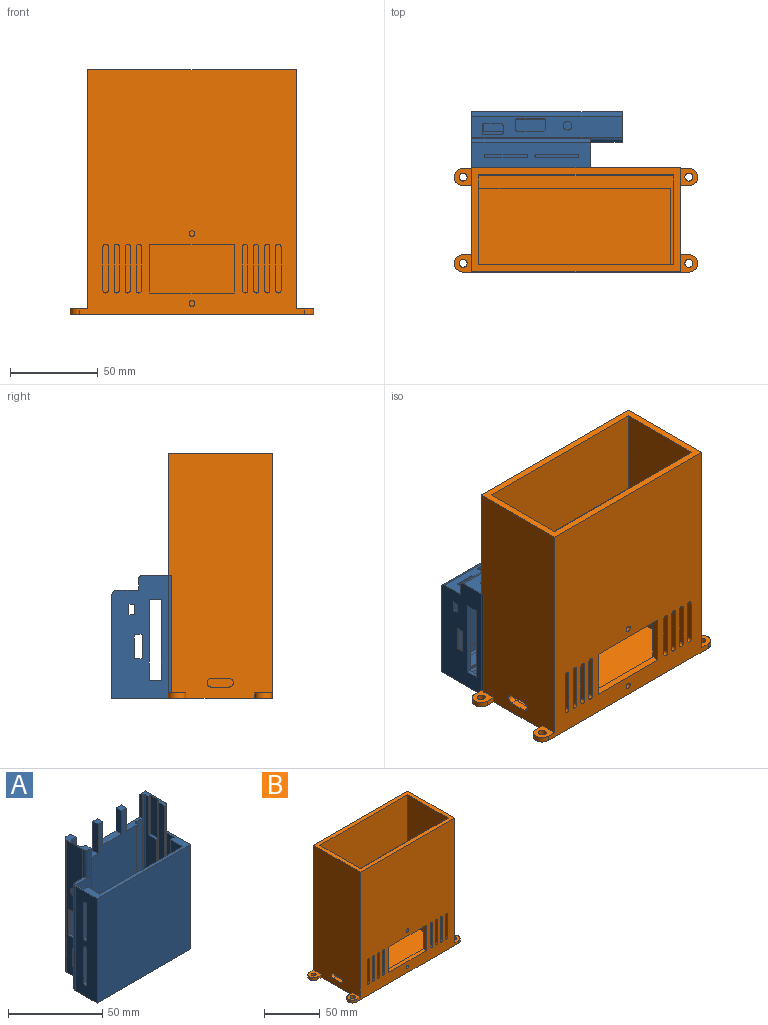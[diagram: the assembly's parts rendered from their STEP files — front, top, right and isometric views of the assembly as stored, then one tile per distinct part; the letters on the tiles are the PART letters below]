
ASSEMBLY  parts=2 mates=1
PART A: 148 faces, bbox 70.8x34.6x86.2 mm
  f0: plane 66x11mm, normal (1,0,0), area 577.7mm2, adj f3,f6,f10,f120,f130,f131,f132,f133
  f1: plane 41x1.75mm, normal (1,0,0), area 71.8mm2, adj f6,f7,f10,f143
  f2: plane 41x1.75mm, normal (-1,0,0), area 71.7mm2, adj f4,f5,f10,f147
  f3: plane 70.4x19.59mm, normal (0,0,1), area 249.6mm2, adj f0,f11,f30,f115,f116,f117,f120,f121
  f4: plane 41x2mm, normal (0,1,0), area 82mm2, adj f2,f10,f117,f147
  f5: plane 41x2mm, normal (0,-1,0), area 82mm2, adj f2,f10,f118,f147
  f6: plane 41x2mm, normal (0,1,0), area 82mm2, adj f0,f1,f10,f143
  f7: plane 41x2mm, normal (0,-1,0), area 82mm2, adj f1,f10,f119,f143
  f8: plane 69.5x5mm, normal (0,-1,0), area 281.5mm2, adj f24,f52,f54,f61,f63,f129
  f9: plane 70.4x34.2mm, normal (0,0,-1), area 1867.4mm2, adj f30,f31,f32,f36,f37,f38,f64,f92
  f10: plane 66x15mm, normal (0,0,1), area 613.2mm2, adj f0,f1,f2,f4,f5,f6,f7,f11
  f11: plane 83.8x11.7mm, normal (0,-1,0), area 674.1mm2, adj f3,f10,f13,f94,f119,f139,f141,f143
  f12: plane 85x4.48mm, normal (-1,0,0), area 369.3mm2, adj f24,f27,f35,f45,f79,f112,f114,f140
  f13: plane 17.2x5.6mm, normal (0,0,1), area 46.4mm2, adj f11,f15,f16,f21,f26,f31,f32,f44
  f14: plane 79.71x8.38mm, normal (-1,0,0), area 504.3mm2, adj f24,f34,f46,f61,f78,f104,f105
  f15: plane 85.1x50.2mm, normal (0,-1,0), area 3518.2mm2, adj f13,f20,f21,f25,f26,f27,f29,f50
  f16: plane 34.45x6.5mm, normal (1,0,0), area 199.8mm2, adj f13,f18,f19,f48,f49,f81
  f17: cone r=1.4mm half-angle=45deg, axis (1,0,0), area 0.8mm2, adj f20,f26,f72,f76,f98
  f18: cone r=3.25mm half-angle=45deg, axis (1,0,0), area 9.7mm2, adj f16,f26,f81,f82
  f19: cylinder r=2.5mm len=5mm, axis (1,0,0), area 12.6mm2, adj f16,f32
  f20: cylinder r=5mm len=6.38mm, axis (0,1,0), area 50.4mm2, adj f15,f17,f26,f27,f72,f80
  f21: cylinder r=1mm len=44.27mm, axis (0,0,-1), area 44.1mm2, adj f13,f15,f26,f82,f83,f86,f88
  f22: plane 5.42x4.59mm, normal (0,1,0), area 18.3mm2, adj f23,f27,f75,f77,f94,f97
  f23: plane 5.34x2.25mm, normal (1,0,0), area 9mm2, adj f22,f27,f47,f72,f75,f80
  f24: plane 17.2x4mm, normal (0,0,1), area 31.1mm2, adj f8,f12,f14,f30,f31,f33,f35,f54
  f25: plane 4.1x3.4mm, normal (0,0,1), area 13.9mm2, adj f15,f31,f56,f60
  f26: plane 80x8.63mm, normal (1,0,0), area 201.6mm2, adj f13,f15,f17,f18,f20,f21,f44,f81
  f27: plane 58.5x15.6mm, normal (0,0,1), area 568.3mm2, adj f12,f15,f20,f22,f23,f33,f34,f35
  f28: plane 7x5mm, normal (0,-1,0), area 22.5mm2, adj f46,f61,f63,f127
  f29: plane 4.1x3.9mm, normal (0,0,1), area 16mm2, adj f15,f31,f53,f57
  f30: plane 85.8x34.2mm, normal (1,0,0), area 2585.6mm2, adj f3,f9,f24,f31,f121,f140
  f31: plane 85.8x59.1mm, normal (0,1,0), area 4281.4mm2, adj f9,f13,f24,f25,f29,f30,f52,f53
  f32: plane 85.8x12mm, normal (-1,0,0), area 818mm2, adj f9,f13,f19,f39,f40,f41,f42,f64
  f33: plane 85x1.75mm, normal (-1,0,0), area 148.8mm2, adj f24,f27,f34,f35,f102
  f34: plane 60x6.09mm, normal (0,-1,0), area 62mm2, adj f14,f27,f33,f78,f105
  f35: plane 85x6.09mm, normal (0,1,0), area 82mm2, adj f12,f24,f27,f33,f79
  f36: plane 3.58x0.8mm, normal (-1,0,0), area 2.9mm2, adj f9,f27,f93,f114
  f37: plane 12x0.8mm, normal (0,-1,0), area 9.6mm2, adj f9,f27,f92,f93
  f38: plane 3.58x0.8mm, normal (1,0,0), area 2.9mm2, adj f9,f27,f92,f114
  f39: plane 5.4x1.2mm, normal (0,0,1), area 6.5mm2, adj f32,f67,f68,f85
  f40: plane 15.4x1.6mm, normal (0,-1,0), area 24.6mm2, adj f32,f50,f65,f68
  f41: plane 5.4x1.24mm, normal (0,0,-1), area 6.5mm2, adj f32,f65,f66,f88,f90
  f42: plane 15.4x1.2mm, normal (0,1,0), area 18.5mm2, adj f32,f66,f67,f89
  f43: cylinder r=5mm len=4.39mm, axis (0,-1,0), area 12.1mm2, adj f27,f77,f94,f110,f111
  f44: plane 68.42x2.89mm, normal (0,1,0), area 164mm2, adj f13,f26,f74,f94,f95,f101
  f45: plane 6.42x6.42mm, normal (-0.71,0,0.71), area 19.8mm2, adj f12,f27,f79,f112,f113
  f46: plane 9.3x6.42mm, normal (-0.71,0,0.71), area 75mm2, adj f14,f27,f28,f61,f78
  f47: plane 4.5x4.5mm, normal (0,-1,0), area 15.9mm2, adj f23,f27,f80
  f48: plane 31.2x0.48mm, normal (0,-1,0), area 15mm2, adj f13,f16,f49,f83
  f49: cylinder r=3.25mm len=2.33mm, axis (1,0,0), area 0.6mm2, adj f16,f48,f82
  f50: plane 16.26x0.13mm, normal (-1,0,0), area 2mm2, adj f15,f40,f65,f68
  f51: plane 70x0.5mm, normal (1,0,0), area 35mm2, adj f27,f52,f62,f63
  f52: plane 14.1x4.1mm, normal (0,0,1), area 44.3mm2, adj f8,f15,f31,f51,f53,f54,f62,f63
  f53: plane 15x4.1mm, normal (1,0,0), area 61.5mm2, adj f15,f29,f31,f52
  f54: plane 15x1.6mm, normal (-1,0,0), area 24mm2, adj f8,f24,f31,f52
  f55: plane 14.1x4.1mm, normal (0,0,1), area 57.8mm2, adj f15,f31,f56,f57
  f56: plane 15x4.1mm, normal (1,0,0), area 61.5mm2, adj f15,f25,f31,f55
  f57: plane 15x4.1mm, normal (-1,0,0), area 61.5mm2, adj f15,f29,f31,f55
  f58: plane 16.6x4.1mm, normal (0,0,1), area 68.1mm2, adj f15,f31,f59,f60
  f59: plane 19x4.1mm, normal (1,0,0), area 77.9mm2, adj f13,f15,f31,f58
  f60: plane 19x4.1mm, normal (-1,0,0), area 77.9mm2, adj f15,f25,f31,f58
  f61: cylinder r=1mm len=80mm, axis (0,0,-1), area 117mm2, adj f8,f14,f24,f28,f46,f126,f127,f129
  f62: cylinder r=1mm len=70mm, axis (0,0,1), area 110mm2, adj f15,f27,f51,f52
  f63: cylinder r=1mm len=70mm, axis (0,0,1), area 108.2mm2, adj f8,f27,f28,f51,f52,f127,f128,f129
  f64: cylinder r=2.6mm len=85.8mm, axis (0,0,-1), area 350.4mm2, adj f9,f13,f31,f32
  f65: cylinder r=0.8mm len=2.19mm, axis (1,0,0), area 2.1mm2, adj f15,f32,f40,f41,f50,f86
  f66: cylinder r=0.8mm len=1.2mm, axis (1,0,0), area 1.5mm2, adj f32,f41,f42,f91
  f67: cylinder r=0.8mm len=1.2mm, axis (1,0,0), area 1.5mm2, adj f32,f39,f42,f87
  f68: cylinder r=0.8mm len=1.6mm, axis (1,0,0), area 1.7mm2, adj f15,f32,f39,f40,f50,f84
  f69: plane 10x3.6mm, normal (0,1,0), area 36mm2, adj f32,f74,f75,f96
  f70: plane 4.2x1.2mm, normal (0,0,-1), area 5mm2, adj f32,f73,f74,f100
  f71: plane 10x1.2mm, normal (0,-1,0), area 12mm2, adj f32,f73,f76,f98
  f72: plane 4.5x1.9mm, normal (0,0,1), area 6.5mm2, adj f17,f20,f23,f32,f75,f76
  f73: cylinder r=1mm len=1.2mm, axis (1,0,0), area 1.9mm2, adj f32,f70,f71,f99
  f74: cylinder r=1mm len=3.6mm, axis (1,0,0), area 3.6mm2, adj f32,f44,f69,f70,f95,f101
  f75: cylinder r=1mm len=3.6mm, axis (1,0,0), area 4mm2, adj f22,f23,f32,f69,f72,f97
  f76: cylinder r=1mm len=1.2mm, axis (1,0,0), area 1.9mm2, adj f17,f32,f71,f72
  f77: cone r=4.5mm half-angle=45deg, axis (0,-1,0), area 3.5mm2, adj f22,f27,f43,f94
  f78: plane 6x6mm, normal (-0.5,-0.71,0.5), area 5.6mm2, adj f14,f27,f34,f46
  f79: plane 6x6mm, normal (-0.5,0.71,0.5), area 5.6mm2, adj f12,f27,f35,f45
  f80: cone r=4.5mm half-angle=45deg, axis (0,1,0), area 5.3mm2, adj f20,f23,f27,f47
  f81: plane 31.2x0.8mm, normal (0.71,0.71,0), area 35.3mm2, adj f13,f16,f18,f26
  f82: bspline ~2.9x1.24mm, area 2.4mm2, adj f18,f21,f49,f83
  f83: plane 31.2x0.59mm, normal (0.4,-0.92,0), area 20mm2, adj f13,f21,f48,f82
  f84: cone r=1.2mm half-angle=45deg, axis (1,0,0), area 0.4mm2, adj f15,f26,f68,f85
  f85: plane 5.4x0.4mm, normal (0.71,0,0.71), area 3.1mm2, adj f26,f39,f84,f87
  f86: bspline ~1.42x0.84mm, area 0.6mm2, adj f15,f21,f65,f88
  f87: cone r=1.2mm half-angle=45deg, axis (1,0,0), area 0.9mm2, adj f26,f67,f85,f89
  f88: cone r=1.4mm half-angle=45deg, axis (0,0,-1), area 0.2mm2, adj f21,f41,f86,f90
  f89: plane 15.4x0.4mm, normal (0.71,0.71,0), area 8.7mm2, adj f26,f42,f87,f91
  f90: plane 5.08x0.4mm, normal (0.71,0,-0.71), area 2.9mm2, adj f26,f41,f88,f91
  f91: cone r=1.2mm half-angle=45deg, axis (1,0,0), area 0.9mm2, adj f26,f66,f89,f90
  f92: cylinder r=1mm len=1mm, axis (0,0,-1), area 1.3mm2, adj f9,f27,f37,f38
  f93: cylinder r=1mm len=1mm, axis (0,0,-1), area 1.3mm2, adj f9,f27,f36,f37
  f94: plane 85.02x4.49mm, normal (1,0,0), area 364.7mm2, adj f11,f13,f22,f27,f43,f44,f77,f95
  f95: cone r=1.4mm half-angle=45deg, axis (1,0,0), area 0.6mm2, adj f44,f74,f94,f96
  f96: plane 10x0.4mm, normal (0.71,0.71,0), area 5.7mm2, adj f69,f94,f95,f97
  f97: cone r=1.4mm half-angle=45deg, axis (1,0,0), area 0.6mm2, adj f22,f75,f94,f96
  f98: plane 10x0.4mm, normal (0.71,-0.71,0), area 5.7mm2, adj f17,f26,f71,f99
  f99: cone r=1.4mm half-angle=45deg, axis (1,0,0), area 1.1mm2, adj f26,f73,f98,f100
  f100: plane 4.2x0.4mm, normal (0.71,0,-0.71), area 2.4mm2, adj f26,f70,f99,f101
  f101: cone r=1.4mm half-angle=45deg, axis (1,0,0), area 0.5mm2, adj f26,f44,f74,f100
  f102: plane 25x0.8mm, normal (0,1,0), area 20mm2, adj f24,f33,f103,f105
  f103: plane 25x6.3mm, normal (-1,0,0), area 157.5mm2, adj f24,f102,f104,f105
  f104: plane 25x1.6mm, normal (0,-1,0), area 40mm2, adj f14,f24,f103,f105
  f105: plane 6.3x1.6mm, normal (0,0,1), area 10.1mm2, adj f14,f34,f102,f103,f104
  f106: plane 3x0.8mm, normal (1,0,0), area 2.4mm2, adj f9,f27,f107,f108
  f107: plane 5.92x0.8mm, normal (0,1,0), area 4.7mm2, adj f9,f27,f106,f109
  f108: plane 5.92x0.8mm, normal (0,-1,0), area 4.7mm2, adj f9,f27,f106,f109
  f109: plane 3x0.8mm, normal (-1,0,0), area 2.4mm2, adj f9,f27,f107,f108
  f110: cylinder r=1mm len=4.39mm, axis (0,0,1), area 6.3mm2, adj f27,f43,f94,f111
  f111: plane 3.67x1.6mm, normal (0,-1,0), area 4.1mm2, adj f27,f43,f110
  f112: cylinder r=1mm len=6mm, axis (0,0,1), area 8.6mm2, adj f12,f27,f45,f113
  f113: plane 5x5mm, normal (0,-1,0), area 12.5mm2, adj f27,f45,f112
  f114: plane 55.3x43mm, normal (0,1,0), area 159.6mm2, adj f9,f10,f12,f27,f36,f38,f94,f118
  f115: plane 68x16.4mm, normal (-1,0,0), area 1016.9mm2, adj f3,f9,f121,f130,f131,f132,f133,f134
  f116: plane 68x6.17mm, normal (0,1,0), area 419.6mm2, adj f3,f9,f138,f139
  f117: plane 66x11mm, normal (-1,0,0), area 676mm2, adj f3,f4,f10,f120,f145,f147
  f118: plane 41x2.25mm, normal (-1,0,0), area 92.3mm2, adj f5,f10,f114,f147
  f119: plane 41x2.25mm, normal (1,0,0), area 92.3mm2, adj f7,f10,f11,f143
  f120: plane 66x62mm, normal (0,1,0), area 4092mm2, adj f0,f3,f10,f117
  f121: plane 70.4x68mm, normal (0,-1,0), area 4787.2mm2, adj f3,f9,f30,f115
  f122: plane 7x2mm, normal (-1,0,0), area 14mm2, adj f9,f10,f123,f124
  f123: plane 46.25x2mm, normal (0,-1,0), area 92.5mm2, adj f9,f10,f122,f125
  f124: plane 46.25x2mm, normal (0,1,0), area 92.5mm2, adj f9,f10,f122,f125
  f125: plane 7x2mm, normal (1,0,0), area 14mm2, adj f9,f10,f123,f124
  f126: plane 8.5x2mm, normal (-1,0,0), area 17mm2, adj f31,f61,f127,f129
  f127: plane 6x2mm, normal (0,0,1), area 9.7mm2, adj f28,f31,f61,f63,f126,f128
  f128: plane 8.5x1.62mm, normal (1,0,0), area 13.8mm2, adj f31,f63,f127,f129
  f129: plane 6x2mm, normal (0,0,-1), area 9.7mm2, adj f8,f31,f61,f63,f126,f128
  f130: cylinder r=1mm len=4mm, axis (-1,0,0), area 12.6mm2, adj f0,f115,f131,f133
  f131: plane 23x4mm, normal (0,-1,0), area 92mm2, adj f0,f115,f130,f132
  f132: cylinder r=1mm len=4mm, axis (-1,0,0), area 12.6mm2, adj f0,f115,f131,f133
  f133: plane 23x4mm, normal (0,1,0), area 92mm2, adj f0,f115,f130,f132
  f134: cylinder r=1mm len=4mm, axis (-1,0,0), area 12.6mm2, adj f0,f115,f135,f137
  f135: plane 23x4mm, normal (0,-1,0), area 92mm2, adj f0,f115,f134,f136
  f136: cylinder r=1mm len=4mm, axis (-1,0,0), area 12.6mm2, adj f0,f115,f135,f137
  f137: plane 23x4mm, normal (0,1,0), area 92mm2, adj f0,f115,f134,f136
  f138: cylinder r=2.6mm len=68mm, axis (0,0,-1), area 277.7mm2, adj f3,f9,f115,f116
  f139: cylinder r=2.6mm len=85.8mm, axis (0,0,1), area 113.9mm2, adj f3,f9,f11,f13,f32,f116
  f140: cylinder r=2.6mm len=17.8mm, axis (0,0,1), area 69.1mm2, adj f3,f12,f24,f30
  f141: plane 25x6mm, normal (1,0,0), area 150mm2, adj f3,f11,f142,f143
  f142: plane 25x3mm, normal (0,1,0), area 75mm2, adj f0,f3,f141,f143
  f143: plane 6x3mm, normal (0,0,1), area 14.5mm2, adj f0,f1,f6,f7,f11,f119,f141,f142
  f144: plane 25x1mm, normal (0,-1,0), area 25mm2, adj f3,f12,f146,f147
  f145: plane 25x3mm, normal (0,1,0), area 75mm2, adj f3,f117,f146,f147
  f146: plane 25x6mm, normal (-1,0,0), area 150mm2, adj f3,f144,f145,f147
  f147: plane 6x3mm, normal (0,0,1), area 14.5mm2, adj f2,f4,f5,f114,f117,f118,f144,f145
PART B: 72 faces, bbox 139x59.3x139.7 mm
  f0: plane 139.7x59.29mm, normal (-1,0,0), area 8153.5mm2, adj f3,f5,f8,f10,f52,f53,f54,f55
  f1: plane 138.7x51.29mm, normal (1,0,0), area 6374.8mm2, adj f2,f4,f6,f10,f11,f13,f52,f53
  f2: plane 138.7x110.98mm, normal (0,1,0), area 13268.1mm2, adj f1,f4,f9,f10,f11,f12,f14,f15
  f3: plane 139.7x128.98mm, normal (0,-1,0), area 14638.3mm2, adj f0,f5,f7,f10,f14,f15,f16,f17
  f4: plane 109.71x43.67mm, normal (0,0,1), area 4791.3mm2, adj f1,f2,f12,f13
  f5: plane 138.98x59.29mm, normal (0,0,-1), area 7348.1mm2, adj f0,f3,f7,f8,f56,f57,f59,f60
  f6: plane 110.98x50.8mm, normal (0,-1,0), area 5637.9mm2, adj f1,f9,f10,f11
  f7: plane 139.7x59.29mm, normal (1,0,0), area 8223.1mm2, adj f3,f5,f8,f10,f56,f58,f59,f61
  f8: plane 139.7x128.98mm, normal (0,1,0), area 16651.8mm2, adj f0,f5,f7,f10,f58,f64,f68,f71
  f9: plane 51.29x50.8mm, normal (-1,0,0), area 2605.6mm2, adj f2,f6,f10,f11
  f10: plane 118.98x59.29mm, normal (0,0,1), area 1362.2mm2, adj f0,f1,f2,f3,f6,f7,f8,f9
  f11: plane 110.98x51.29mm, normal (0,0,1), area 901.1mm2, adj f1,f2,f6,f9,f12,f13
  f12: plane 87.9x43.67mm, normal (-1,0,0), area 3838.8mm2, adj f2,f4,f11,f13
  f13: plane 109.71x87.9mm, normal (0,-1,0), area 9643.7mm2, adj f1,f4,f11,f12
  f14: plane 48.01x4mm, normal (0,0,1), area 192mm2, adj f2,f3,f15,f16
  f15: plane 27.94x4mm, normal (1,0,0), area 111.8mm2, adj f2,f3,f14,f17
  f16: plane 27.94x4mm, normal (-1,0,0), area 111.8mm2, adj f2,f3,f14,f17
  f17: plane 48.01x4mm, normal (0,0,-1), area 192mm2, adj f2,f3,f15,f16
  f18: plane 24.94x4mm, normal (1,0,0), area 99.8mm2, adj f2,f3,f19,f20
  f19: cylinder r=1.5mm len=4mm, axis (0,-1,0), area 18.8mm2, adj f2,f3,f18,f21
  f20: cylinder r=1.5mm len=4mm, axis (0,-1,0), area 18.8mm2, adj f2,f3,f18,f21
  f21: plane 24.94x4mm, normal (-1,0,0), area 99.8mm2, adj f2,f3,f19,f20
  f22: cylinder r=1.5mm len=4mm, axis (0,-1,0), area 18.8mm2, adj f2,f3,f23,f24
  f23: plane 24.94x4mm, normal (-1,0,0), area 99.8mm2, adj f2,f3,f22,f25
  f24: plane 24.94x4mm, normal (1,0,0), area 99.8mm2, adj f2,f3,f22,f25
  f25: cylinder r=1.5mm len=4mm, axis (0,-1,0), area 18.8mm2, adj f2,f3,f23,f24
  f26: cylinder r=1.65mm len=4mm, axis (0,-1,0), area 41.5mm2, adj f2,f3
  f27: cylinder r=1.65mm len=4mm, axis (0,-1,0), area 41.5mm2, adj f2,f3
  f28: plane 24.94x4mm, normal (1,0,0), area 99.8mm2, adj f2,f3,f29,f31
  f29: cylinder r=1.5mm len=4mm, axis (0,-1,0), area 18.8mm2, adj f2,f3,f28,f30
  f30: plane 24.94x4mm, normal (-1,0,0), area 99.8mm2, adj f2,f3,f29,f31
  f31: cylinder r=1.5mm len=4mm, axis (0,-1,0), area 18.8mm2, adj f2,f3,f28,f30
  f32: plane 24.94x4mm, normal (1,0,0), area 99.8mm2, adj f2,f3,f33,f35
  f33: cylinder r=1.5mm len=4mm, axis (0,-1,0), area 18.8mm2, adj f2,f3,f32,f34
  f34: plane 24.94x4mm, normal (-1,0,0), area 99.8mm2, adj f2,f3,f33,f35
  f35: cylinder r=1.5mm len=4mm, axis (0,-1,0), area 18.8mm2, adj f2,f3,f32,f34
  f36: plane 24.94x4mm, normal (1,0,0), area 99.8mm2, adj f2,f3,f37,f38
  f37: cylinder r=1.5mm len=4mm, axis (0,-1,0), area 18.8mm2, adj f2,f3,f36,f39
  f38: cylinder r=1.5mm len=4mm, axis (0,-1,0), area 18.8mm2, adj f2,f3,f36,f39
  f39: plane 24.94x4mm, normal (-1,0,0), area 99.8mm2, adj f2,f3,f37,f38
  f40: plane 24.94x4mm, normal (1,0,0), area 99.8mm2, adj f2,f3,f41,f42
  f41: cylinder r=1.5mm len=4mm, axis (0,-1,0), area 18.8mm2, adj f2,f3,f40,f43
  f42: cylinder r=1.5mm len=4mm, axis (0,-1,0), area 18.8mm2, adj f2,f3,f40,f43
  f43: plane 24.94x4mm, normal (-1,0,0), area 99.8mm2, adj f2,f3,f41,f42
  f44: cylinder r=1.5mm len=4mm, axis (0,-1,0), area 18.8mm2, adj f2,f3,f45,f46
  f45: plane 24.94x4mm, normal (-1,0,0), area 99.8mm2, adj f2,f3,f44,f47
  f46: plane 24.94x4mm, normal (1,0,0), area 99.8mm2, adj f2,f3,f44,f47
  f47: cylinder r=1.5mm len=4mm, axis (0,-1,0), area 18.8mm2, adj f2,f3,f45,f46
  f48: cylinder r=1.5mm len=4mm, axis (0,-1,0), area 18.8mm2, adj f2,f3,f49,f51
  f49: plane 24.94x4mm, normal (-1,0,0), area 99.8mm2, adj f2,f3,f48,f50
  f50: cylinder r=1.5mm len=4mm, axis (0,-1,0), area 18.8mm2, adj f2,f3,f49,f51
  f51: plane 24.94x4mm, normal (1,0,0), area 99.8mm2, adj f2,f3,f48,f50
  f52: plane 10x4mm, normal (0,0,-1), area 40mm2, adj f0,f1,f54,f55
  f53: plane 10x4mm, normal (0,0,1), area 40mm2, adj f0,f1,f54,f55
  f54: cylinder r=2.5mm len=5mm, axis (1,0,0), area 31.4mm2, adj f0,f1,f52,f53
  f55: cylinder r=2.5mm len=5mm, axis (-1,0,0), area 31.4mm2, adj f0,f1,f52,f53
  f56: plane 5x3mm, normal (0,-1,0), area 15mm2, adj f5,f7,f58,f68
  f57: cylinder r=2.25mm len=4.5mm, axis (0,0,-1), area 42.4mm2, adj f5,f58
  f58: plane 10x10mm, normal (0,0,1), area 73.4mm2, adj f7,f8,f56,f57,f68
  f59: plane 5x3mm, normal (0,1,0), area 15mm2, adj f5,f7,f61,f69
  f60: cylinder r=2.25mm len=4.5mm, axis (0,0,-1), area 42.4mm2, adj f5,f61
  f61: plane 10x10mm, normal (0,0,1), area 73.4mm2, adj f3,f7,f59,f60,f69
  f62: plane 5x3mm, normal (0,-1,0), area 15mm2, adj f0,f5,f64,f71
  f63: cylinder r=2.25mm len=4.5mm, axis (0,0,-1), area 42.4mm2, adj f5,f64
  f64: plane 10x10mm, normal (0,0,1), area 73.4mm2, adj f0,f8,f62,f63,f71
  f65: plane 5x3mm, normal (0,1,0), area 15mm2, adj f0,f5,f67,f70
  f66: cylinder r=2.25mm len=4.5mm, axis (0,0,-1), area 42.4mm2, adj f5,f67
  f67: plane 10x10mm, normal (0,0,1), area 73.4mm2, adj f0,f3,f65,f66,f70
  f68: cylinder r=5mm len=10mm, axis (0,0,1), area 47.1mm2, adj f5,f8,f56,f58
  f69: cylinder r=5mm len=10mm, axis (0,0,1), area 47.1mm2, adj f3,f5,f59,f61
  f70: cylinder r=5mm len=10mm, axis (0,0,-1), area 47.1mm2, adj f3,f5,f65,f67
  f71: cylinder r=5mm len=10mm, axis (0,0,-1), area 47.1mm2, adj f5,f8,f62,f64
PLACE A rot(axis=(0,1,0),90deg) t=(-100.39,72.36,25.79)mm
PLACE B t=(-41.7,19.12,-5.06)mm
MATE fastened A.f9 <-> B.f0  axis (-1,0,0) through (-101.19,46.76,-5.06)mm
